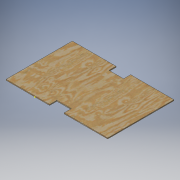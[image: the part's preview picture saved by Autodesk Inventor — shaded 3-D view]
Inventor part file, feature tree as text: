
AUTODESK INVENTOR PART (.ipt)
format: ipt  version: 2016 (Build 200138000, 138)  size: 128,512 bytes
history: native  units: in
note: dims shown in document units (in); Inventor stores cm internally (conversion verified against a paired STEP export)
features: sketch x4, extrude x2
ambient origin geometry x8: Origin, YZ Plane, XZ Plane, XY Plane, X Axis, Y Axis, Z Axis, Center Point
bodies: Solid1 (feature_tree)
feature tree (6):
  sketch  "Sketch1"  dims[d0=18.25in d1=28.0in]
  extrude  "Extrusion1"  Depth=28.0in
  extrude  "Extrusion2"  Depth=2.0in
  sketch  "Sketch4"  dims[d6=12.0in d8=2.0in d9=4.0in d10=0.0in d11=0.25in d12=0.0in]
  sketch  "Sketch2"  dims[d2=0.25in d3=0.0in d4=2.0in]
  sketch  "Sketch3"  dims[d5=4.0in]
